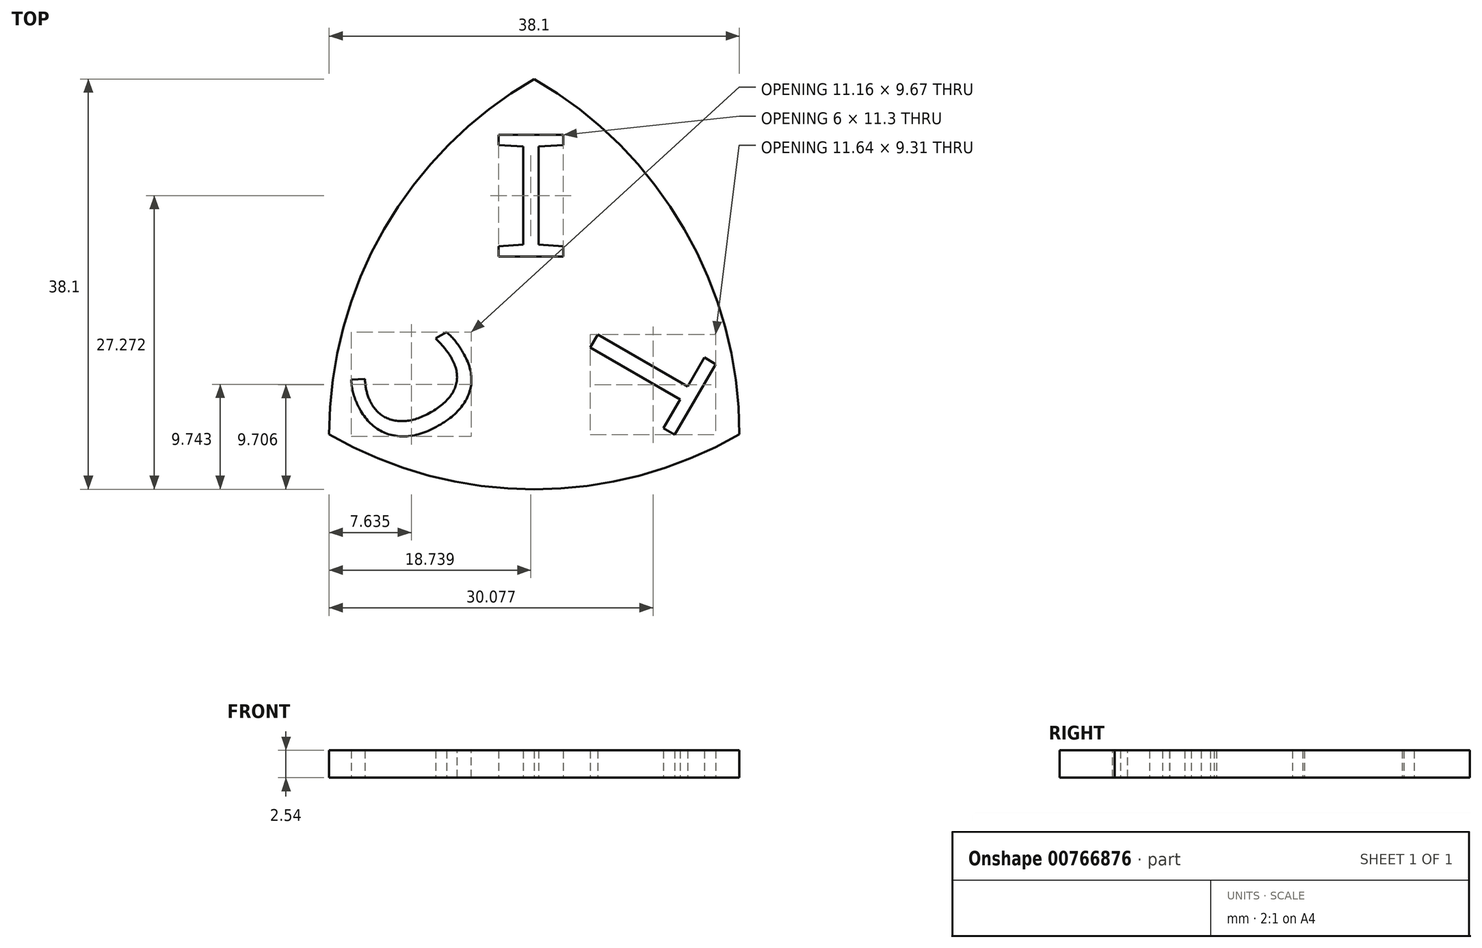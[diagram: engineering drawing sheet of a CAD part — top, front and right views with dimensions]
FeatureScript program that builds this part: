
annotation { "Feature Type Name" : "Feature", "Feature Type Description" : "" }
export const myFeature = defineFeature(function(context is Context, id is Id, definition is map)
    precondition{}
    {
        {
            var Q0;
            Q0=qCreatedBy(makeId("Top.planeOp"),FACE);
            var sketch = newSketch(context, id + "F0", { "sketchPlane" : qUnion([Q0])});
            skCircle(sketch, "E0", {"center": v(0, 0) * mm, "radius": 38.1 * mm});
            skSolve(sketch);
        }
        {
            var Q0;
            Q0=qCreatedBy(makeId("Top.planeOp"),FACE);
            var sketch = newSketch(context, id + "F1", { "sketchPlane" : qUnion([Q0])});
            skCircle(sketch, "E1", {"center": v(-38.1, 0) * mm, "radius": 38.1 * mm});
            skSolve(sketch);
        }
        {
            var Q0;
            Q0=qCreatedBy(makeId("Top.planeOp"),FACE);
            var sketch = newSketch(context, id + "F2", { "sketchPlane" : qUnion([Q0])});
            skCircle(sketch, "E2", {"center": v(-19.05, 33) * mm, "radius": 38.1 * mm});
            skSolve(sketch);
        }
        {
            var Q0;
            Q0 = qSketchRegion(id + "F0", true);
            extrude(context, id + "F3", {"entities" : qUnion([Q0]), "depth" : 2.54 * mm, "offsetDistance" : 25.4 * mm});
        }
        {
            var Q0;
            Q0 = qSketchRegion(id + "F1", true);
            extrude(context, id + "F4", {"entities" : qUnion([Q0]), "depth" : 2.54 * mm, "offsetDistance" : 25.4 * mm});
        }
        {
            var Q0;
            Q0 = qSketchRegion(id + "F2", true);
            extrude(context, id + "F5", {"entities" : qUnion([Q0]), "depth" : 2.54 * mm, "offsetDistance" : 25.4 * mm});
        }
        {
            var Q0;
            Q0=makeQuery(id+"F3.opExtrude","SWEPT_BODY",BODY,{"disambiguationData":[OSD([sQuery(id+"F0.wireOp",EDGE,"E0")])]});
            var Q1;
            Q1=makeQuery(id+"F4.opExtrude","SWEPT_BODY",BODY,{"disambiguationData":[OSD([sQuery(id+"F1.wireOp",EDGE,"E1")])]});
            var Q2;
            Q2=makeQuery(id+"F5.opExtrude","SWEPT_BODY",BODY,{"disambiguationData":[OSD([sQuery(id+"F2.wireOp",EDGE,"E2")])]});
            booleanBodies(context, id + "F6", {"operationType" : BooleanOperationType.INTERSECTION, "tools" : qUnion([Q0, Q1, Q2])});
        }
        {
            var Q0;
            Q0=qCreatedBy(makeId("Top.planeOp"),FACE);
            var sketch = newSketch(context, id + "F7", { "sketchPlane" : qUnion([Q0])});
            skText(sketch, "E3", { "text": "C", "fontName": "DroidSansMono.ttf"});
            skText(sketch, "E4", { "text": "I", "fontName": "DroidSansMono.ttf"});
            skText(sketch, "E5", { "text": "T", "fontName": "DroidSansMono.ttf"});
            const initialGuessF7  = {"E3": [-0.023, 0.00244, -0.48069, 0.8769, 0.01073], "E4": [-0.0241, 0.01652, 1, 0, 0.0114], "E5": [-0.01122, 0.0126, -0.5, -0.86603, 0.01094]};
            skSetInitialGuess(sketch, initialGuessF7);
            skSolve(sketch);
        }
        {
            var Q0;
            Q0 = qSketchRegion(id + "F7", true);
            extrude(context, id + "F8", {"entities" : qUnion([Q0]), "depth" : 2.54 * mm, "offsetDistance" : 25.4 * mm});
        }
        {
            var Q0;
            Q0=makeQuery(id+"F8.opExtrude","SWEPT_BODY",BODY,{"disambiguationData":[OSD([sQuery(id+"F7.wireOp",EDGE,"E3.sketch_text.stroke-0"),sQuery(id+"F7.wireOp",EDGE,"E3.sketch_text.stroke-1"),sQuery(id+"F7.wireOp",EDGE,"E3.sketch_text.stroke-2"),sQuery(id+"F7.wireOp",EDGE,"E3.sketch_text.stroke-3"),sQuery(id+"F7.wireOp",EDGE,"E3.sketch_text.stroke-4"),sQuery(id+"F7.wireOp",EDGE,"E3.sketch_text.stroke-5"),sQuery(id+"F7.wireOp",EDGE,"E3.sketch_text.stroke-6"),sQuery(id+"F7.wireOp",EDGE,"E3.sketch_text.stroke-7"),sQuery(id+"F7.wireOp",EDGE,"E3.sketch_text.stroke-8"),sQuery(id+"F7.wireOp",EDGE,"E3.sketch_text.stroke-9"),sQuery(id+"F7.wireOp",EDGE,"E3.sketch_text.stroke-10"),sQuery(id+"F7.wireOp",EDGE,"E3.sketch_text.stroke-11"),sQuery(id+"F7.wireOp",EDGE,"E3.sketch_text.stroke-12"),sQuery(id+"F7.wireOp",EDGE,"E3.sketch_text.stroke-13")])]});
            var Q1;
            Q1=makeQuery(id+"F8.opExtrude","SWEPT_BODY",BODY,{"disambiguationData":[OSD([sQuery(id+"F7.wireOp",EDGE,"E4.sketch_text.stroke-0"),sQuery(id+"F7.wireOp",EDGE,"E4.sketch_text.stroke-1"),sQuery(id+"F7.wireOp",EDGE,"E4.sketch_text.stroke-2"),sQuery(id+"F7.wireOp",EDGE,"E4.sketch_text.stroke-3"),sQuery(id+"F7.wireOp",EDGE,"E4.sketch_text.stroke-4"),sQuery(id+"F7.wireOp",EDGE,"E4.sketch_text.stroke-5"),sQuery(id+"F7.wireOp",EDGE,"E4.sketch_text.stroke-6"),sQuery(id+"F7.wireOp",EDGE,"E4.sketch_text.stroke-7"),sQuery(id+"F7.wireOp",EDGE,"E4.sketch_text.stroke-8"),sQuery(id+"F7.wireOp",EDGE,"E4.sketch_text.stroke-9"),sQuery(id+"F7.wireOp",EDGE,"E4.sketch_text.stroke-10"),sQuery(id+"F7.wireOp",EDGE,"E4.sketch_text.stroke-11")])]});
            var Q2;
            Q2=makeQuery(id+"F8.opExtrude","SWEPT_BODY",BODY,{"disambiguationData":[OSD([sQuery(id+"F7.wireOp",EDGE,"E5.sketch_text.stroke-0"),sQuery(id+"F7.wireOp",EDGE,"E5.sketch_text.stroke-1"),sQuery(id+"F7.wireOp",EDGE,"E5.sketch_text.stroke-2"),sQuery(id+"F7.wireOp",EDGE,"E5.sketch_text.stroke-3"),sQuery(id+"F7.wireOp",EDGE,"E5.sketch_text.stroke-4"),sQuery(id+"F7.wireOp",EDGE,"E5.sketch_text.stroke-5"),sQuery(id+"F7.wireOp",EDGE,"E5.sketch_text.stroke-6"),sQuery(id+"F7.wireOp",EDGE,"E5.sketch_text.stroke-7")])]});
            var Q3;
            Q3=makeQuery(id+"F6.opBoolean","INTERSECT",BODY,{"derivedFrom":[makeQuery(id+"F3.opExtrude","SWEPT_BODY",BODY,{"disambiguationData":[OSD([sQuery(id+"F0.wireOp",EDGE,"E0")])]}),makeQuery(id+"F4.opExtrude","SWEPT_BODY",BODY,{"disambiguationData":[OSD([sQuery(id+"F1.wireOp",EDGE,"E1")])]}),makeQuery(id+"F5.opExtrude","SWEPT_BODY",BODY,{"disambiguationData":[OSD([sQuery(id+"F2.wireOp",EDGE,"E2")])]})]});
            booleanBodies(context, id + "F9", {"operationType" : BooleanOperationType.SUBTRACTION, "tools" : qUnion([Q0, Q1, Q2]), "targets" : qUnion([Q3]), "keepTools" : true});
        }
    });
